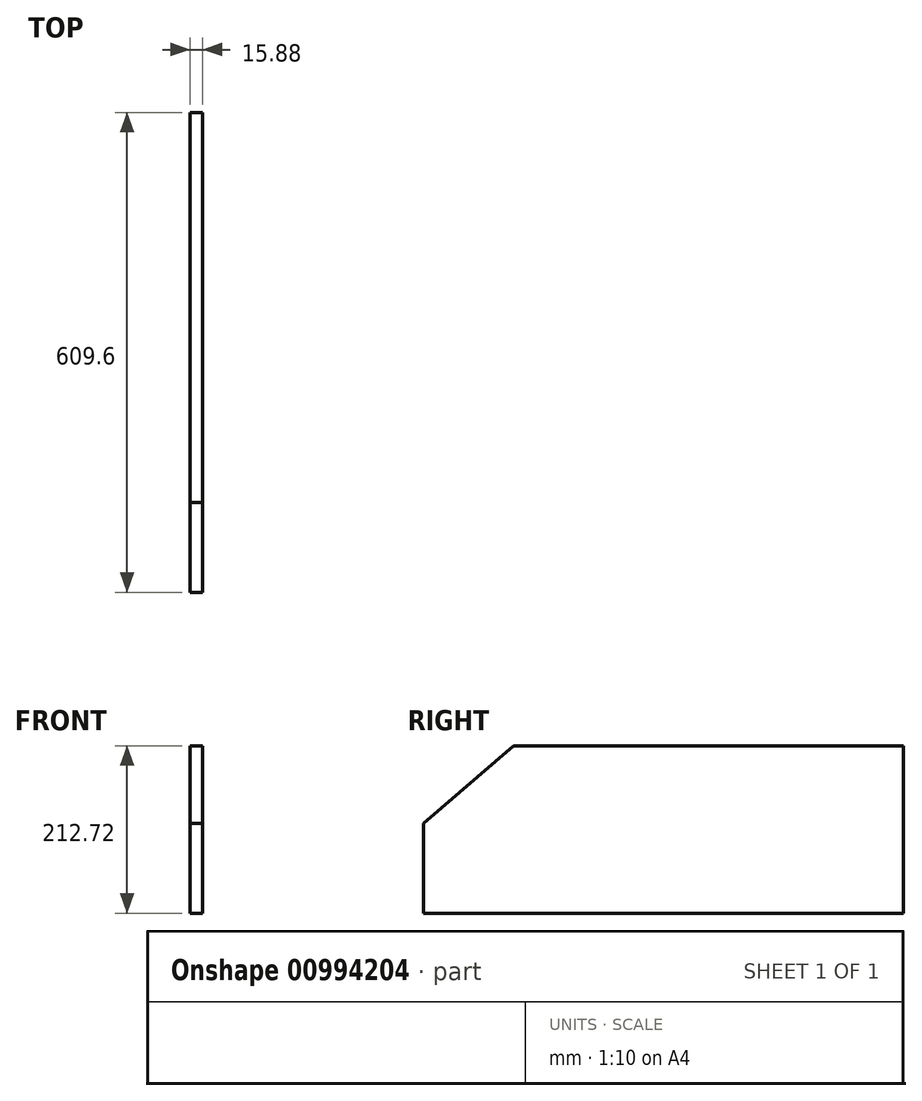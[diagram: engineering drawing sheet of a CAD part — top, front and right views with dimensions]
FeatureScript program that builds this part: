
annotation { "Feature Type Name" : "Feature", "Feature Type Description" : "" }
export const myFeature = defineFeature(function(context is Context, id is Id, definition is map)
    precondition{}
    {
        {
            var Q0;
            Q0=qCreatedBy(makeId("Right.planeOp"),FACE);
            var sketch = newSketch(context, id + "F0", { "sketchPlane" : qUnion([Q0])});
            skLineSegment(sketch, "E0", {"start": v(0, 0) * mm, "end": v(609.6, 0) * mm});
            skLineSegment(sketch, "E1", {"start": v(609.6, 0) * mm, "end": v(609.6, 212.72) * mm});
            skLineSegment(sketch, "E2", {"start": v(609.6, 212.72) * mm, "end": v(114.3, 212.72) * mm});
            skLineSegment(sketch, "E3", {"start": v(114.3, 212.72) * mm, "end": v(0, 114.3) * mm});
            skLineSegment(sketch, "E4", {"start": v(0, 114.3) * mm, "end": v(0, 0) * mm});
            skSolve(sketch);
        }
        {
            var Q0;
            Q0 = qSketchRegion(id + "F0", true);
            extrude(context, id + "F1", {"entities" : qUnion([Q0]), "depth" : 15.88 * mm, "offsetDistance" : 25.4 * mm});
        }
    });
